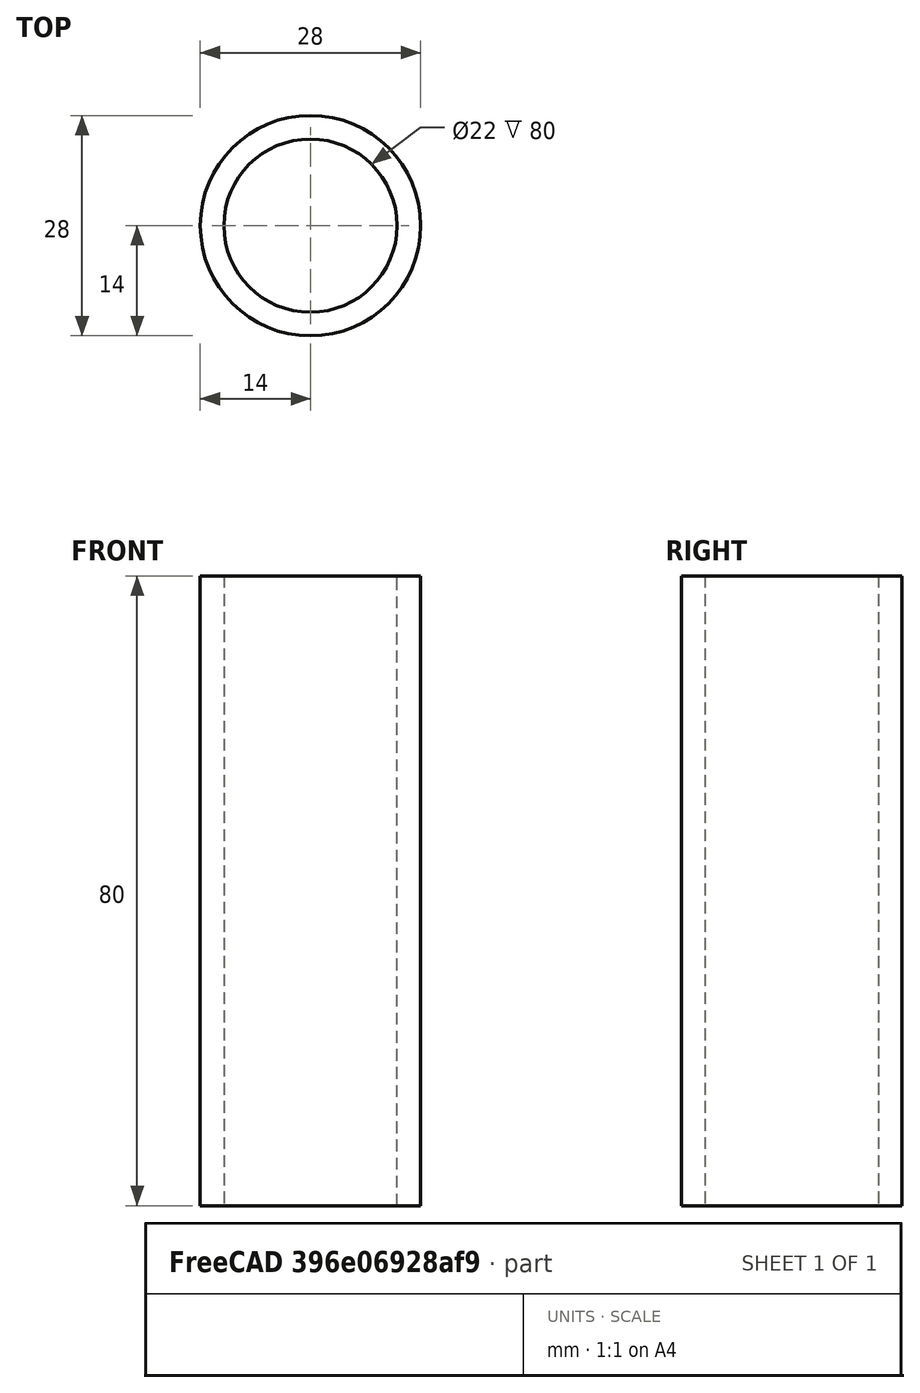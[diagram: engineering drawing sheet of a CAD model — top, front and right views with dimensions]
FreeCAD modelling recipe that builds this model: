
FCSTD DOCUMENT  (FreeCAD 0.19R)
Label: Film_Spool_4
License: All rights reserved
LicenseURL: http://en.wikipedia.org/wiki/All_rights_reserved
objects: Sketcher::SketchObject×1, PartDesign::Pad×1, PartDesign::Body×1
note: 4 computed .brp shape members not serialized (recipe doc carries the construction recipe); baked Part::Feature solids carry a one-line shape summary decoded from their .brp

FEATURE [Sketcher::SketchObject] Sketch
  FullyConstrained = true
  MapMode = 5
  Support = -> [XY_Plane]
  sketch-geometry (2):
    g0: Circle CenterX=0 CenterY=0 CenterZ=0 NormalX=0 NormalY=0 NormalZ=1 AngleXU=0 Radius=11
    g1: Circle CenterX=0 CenterY=0 CenterZ=0 NormalX=0 NormalY=0 NormalZ=1 AngleXU=0 Radius=14
  constraints (4):
    c: Coincident(g0,g-1)
    c: Coincident(g1,g0)
    c: Diameter(g0) = 22
    c: Diameter(g1) = 28
FEATURE [PartDesign::Pad] Pad
  Direction = (1,1,1)
  Length = 80
  Length2 = 100
  Profile = -> Sketch
  Type = 0
FEATURE [PartDesign::Body] Body
  Group = -> [Sketch,Pad]
  Origin = -> Origin
  Tip = -> Pad
